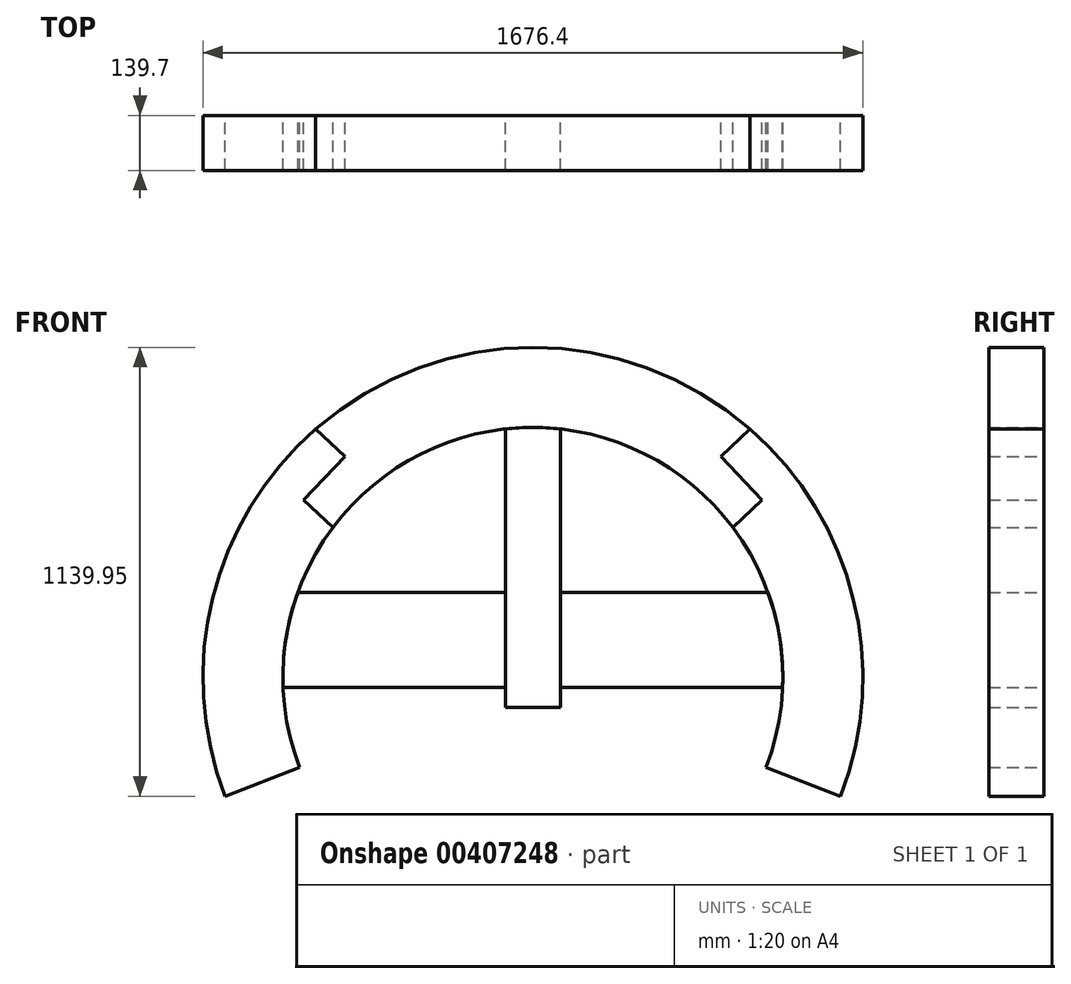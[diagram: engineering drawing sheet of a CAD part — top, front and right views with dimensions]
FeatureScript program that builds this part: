
annotation { "Feature Type Name" : "Feature", "Feature Type Description" : "" }
export const myFeature = defineFeature(function(context is Context, id is Id, definition is map)
    precondition{}
    {
        {
            var Q0;
            Q0=qCreatedBy(makeId("Front.planeOp"),FACE);
            var sketch = newSketch(context, id + "F0", { "sketchPlane" : qUnion([Q0])});
            skArc(sketch, "E0", {"start": v(782, -301.75) * mm, "mid": v(0, 838.2) * mm, "end": v(-782, -301.75) * mm});
            skLineSegment(sketch, "E1", {"start": v(0, 0) * mm, "end": v(0, 838.2) * mm, "construction": true});
            skArc(sketch, "E2", {"start": v(592.42, -228.6) * mm, "mid": v(0, 635) * mm, "end": v(-592.42, -228.6) * mm});
            skLineSegment(sketch, "E3", {"start": v(-592.42, -228.6) * mm, "end": v(-782, -301.75) * mm});
            skLineSegment(sketch, "E4", {"start": v(592.42, -228.6) * mm, "end": v(782, -301.75) * mm});
            skLineSegment(sketch, "E5", {"start": v(-634.5, -25.4) * mm, "end": v(634.5, -25.4) * mm});
            skLineSegment(sketch, "E6", {"start": v(-597.17, 215.9) * mm, "end": v(597.17, 215.9) * mm});
            skLineSegment(sketch, "E7", {"start": v(-69.85, 631.15) * mm, "end": v(-69.85, -76.2) * mm});
            skLineSegment(sketch, "E8.MirrorCS", {"start": v(69.85, 631.15) * mm, "end": v(69.85, -76.2) * mm});
            skLineSegment(sketch, "E9", {"start": v(-69.85, -76.2) * mm, "end": v(69.85, -76.2) * mm});
            skLineSegment(sketch, "E10", {"start": v(-551.45, 631.26) * mm, "end": v(-477.48, 561.6) * mm});
            skLineSegment(sketch, "E11", {"start": v(-477.48, 561.6) * mm, "end": v(-581.96, 450.65) * mm});
            skLineSegment(sketch, "E12", {"start": v(-581.96, 450.65) * mm, "end": v(-508, 381) * mm});
            skLineSegment(sketch, "E13.MirrorCS", {"start": v(581.96, 450.65) * mm, "end": v(508, 381) * mm});
            skLineSegment(sketch, "E14.MirrorCS", {"start": v(477.48, 561.6) * mm, "end": v(581.96, 450.65) * mm});
            skLineSegment(sketch, "E15.MirrorCS", {"start": v(551.45, 631.26) * mm, "end": v(477.48, 561.6) * mm});
            skSolve(sketch);
        }
        {
            var Q0;
            {var subQ0=sQuery(id+"F0.wireOp",EDGE,"E3");Q0=makeQuery(id+"F0.imprint","IMPRINT",FACE,{"disambiguationData":[TD([[makeQuery(id+"F0.imprint","IMPRINT",EDGE,{"derivedFrom":subQ0}),-1.0]])]});}
            extrude(context, id + "F1", {"entities" : qUnion([Q0]), "depth" : 139.7 * mm});
        }
        {
            var Q0;
            {var subQ2=sQuery(id+"F0.wireOp",EDGE,"rozzaD0B-wmKP-oJZg-hCa9-5GciEossttBR");Q0=makeQuery(id+"F0.imprint","IMPRINT",FACE,{"disambiguationData":[TD([[makeQuery(id+"F0.imprint","IMPRINT",EDGE,{"derivedFrom":subQ2}),1.0]])]});}
            var Q1;
            {var subQ0=sQuery(id+"F0.wireOp",EDGE,"E5");var subQ1=sQuery(id+"F0.wireOp",EDGE,"E2");var subQ2=makeQuery(id+"F0.imprint","INTERSECT",VERTEX,{"disambiguationData":[OD(0.0)],"derivedFrom":[subQ1,subQ0]});Q1=makeQuery(id+"F0.imprint","IMPRINT",FACE,{"disambiguationData":[TD([[makeQuery(id+"F0.imprint","IMPRINT",EDGE,{"disambiguationData":[TD([[subQ2,1.0]])],"derivedFrom":subQ1}),1.0]])]});}
            extrude(context, id + "F2", {"entities" : qUnion([Q0, Q1]), "depth" : 139.7 * mm});
        }
        {
            var Q0;
            {var subQ0=sQuery(id+"F0.wireOp",EDGE,"E7");var subQ1=sQuery(id+"F0.wireOp",EDGE,"E2");var subQ2=makeQuery(id+"F0.imprint","INTERSECT",VERTEX,{"derivedFrom":[subQ1,subQ0]});Q0=makeQuery(id+"F0.imprint","IMPRINT",FACE,{"disambiguationData":[TD([[makeQuery(id+"F0.imprint","IMPRINT",EDGE,{"disambiguationData":[TD([[subQ2,1.0]])],"derivedFrom":subQ1}),1.0]])]});}
            var Q1;
            {var subQ0=sQuery(id+"F0.wireOp",EDGE,"E7");var subQ1=sQuery(id+"F0.wireOp",EDGE,"E5");var subQ2=makeQuery(id+"F0.imprint","INTERSECT",VERTEX,{"derivedFrom":[subQ1,subQ0]});Q1=makeQuery(id+"F0.imprint","IMPRINT",FACE,{"disambiguationData":[TD([[makeQuery(id+"F0.imprint","IMPRINT",EDGE,{"disambiguationData":[TD([[subQ2,-1.0]])],"derivedFrom":subQ1}),1.0]])]});}
            var Q2;
            {var subQ5=sQuery(id+"F0.wireOp",EDGE,"E9");Q2=makeQuery(id+"F0.imprint","IMPRINT",FACE,{"disambiguationData":[TD([[makeQuery(id+"F0.imprint","IMPRINT",EDGE,{"derivedFrom":subQ5}),1.0]])]});}
            extrude(context, id + "F3", {"entities" : qUnion([Q0, Q1, Q2]), "depth" : 139.7 * mm});
        }
        {
            var Q0;
            {var subQ5=sQuery(id+"F0.wireOp",EDGE,"E10");Q0=makeQuery(id+"F0.imprint","IMPRINT",FACE,{"disambiguationData":[TD([[makeQuery(id+"F0.imprint","IMPRINT",EDGE,{"derivedFrom":subQ5}),1.0]])]});}
            extrude(context, id + "F4", {"entities" : qUnion([Q0]), "depth" : 139.7 * mm});
        }
        {
            var Q0;
            Q0=makeQuery(id+"F1.opExtrude","SWEPT_BODY",BODY,{"disambiguationData":[OSD([sQuery(id+"F0.wireOp",EDGE,"E0"),sQuery(id+"F0.wireOp",EDGE,"E2"),sQuery(id+"F0.wireOp",EDGE,"E3"),sQuery(id+"F0.wireOp",EDGE,"E10"),sQuery(id+"F0.wireOp",EDGE,"E11"),sQuery(id+"F0.wireOp",EDGE,"E12")])]});
            var Q1;
            Q1=makeQuery(id+"F2.opExtrude","SWEPT_BODY",BODY,{"disambiguationData":[OSD([sQuery(id+"F0.wireOp",EDGE,"E2"),sQuery(id+"F0.wireOp",EDGE,"E5"),sQuery(id+"F0.wireOp",EDGE,"E6"),sQuery(id+"F0.wireOp",EDGE,"E7")])]});
            var Q2;
            Q2=qCreatedBy(makeId("Right.planeOp"),FACE);
            mirror(context, id + "F5", {"entities" : qUnion([Q0, Q1]), "mirrorPlane" : qUnion([Q2])});
        }
    });
